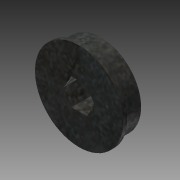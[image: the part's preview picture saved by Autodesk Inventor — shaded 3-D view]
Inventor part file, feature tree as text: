
AUTODESK INVENTOR PART (.ipt)
format: ipt  version: 2014 (Build 180170000, 170)  size: 116,224 bytes
history: native  units: in
note: dims shown in document units (in); Inventor stores cm internally (conversion verified against a paired STEP export)
features: extrude x2, sketch x2
ambient origin geometry x8: Origin, YZ Plane, XZ Plane, XY Plane, X Axis, Y Axis, Z Axis, Center Point
bodies: Solid1 (feature_tree)
feature tree (4):
  extrude  "Extrusion1"  Depth=0.375in
  extrude  "Extrusion2"  Depth=0.055in
  sketch  "Sketch1"  dims[d0=0.375in d1=1.125in]
  sketch  "Sketch2"  dims[d2=0.25in d3=0.0in d4=0.055in d5=0.055in d6=0.0in]
